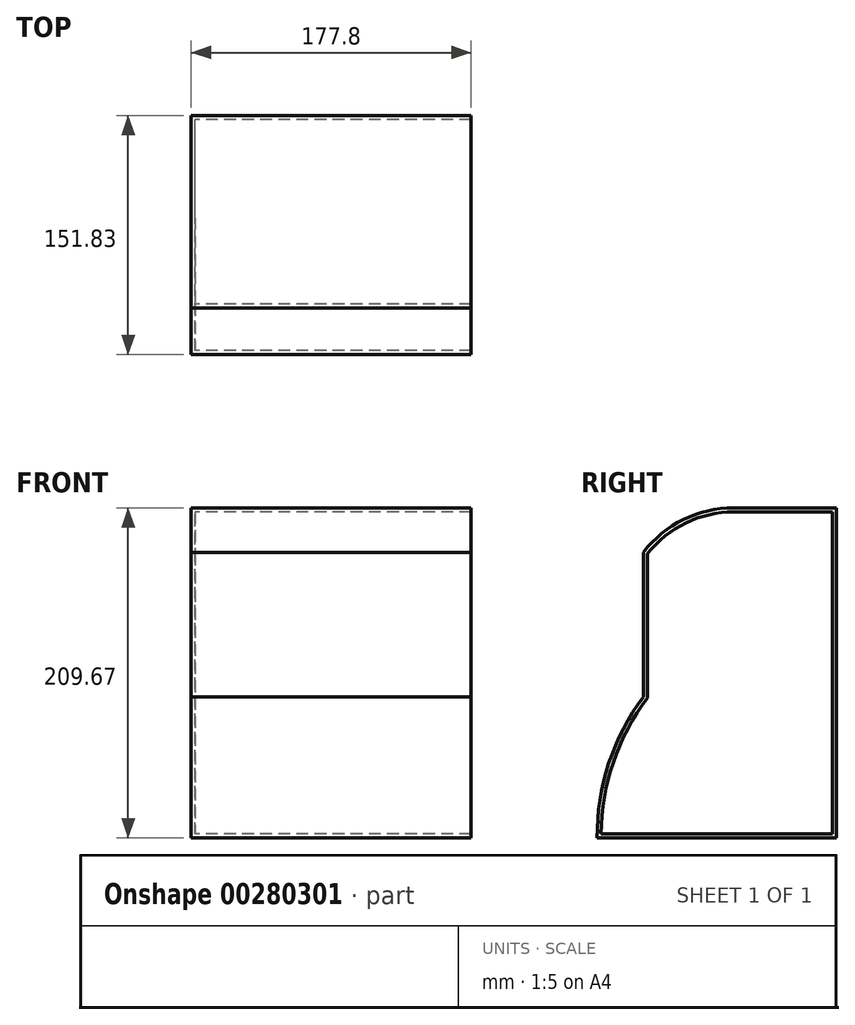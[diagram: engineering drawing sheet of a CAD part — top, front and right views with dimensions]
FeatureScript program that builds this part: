
annotation { "Feature Type Name" : "Feature", "Feature Type Description" : "" }
export const myFeature = defineFeature(function(context is Context, id is Id, definition is map)
    precondition{}
    {
        {
            var Q0;
            Q0=qCreatedBy(makeId("Right.planeOp"),FACE);
            var sketch = newSketch(context, id + "F0", { "sketchPlane" : qUnion([Q0])});
            skArc(sketch, "E0", {"start": v(33.16, 61.72) * mm, "mid": v(1.2, 54.3) * mm, "end": v(-24.2, 33.55) * mm});
            skLineSegment(sketch, "E1", {"start": v(-24.2, 33.55) * mm, "end": v(-24.2, -58.2) * mm});
            skArc(sketch, "E2", {"start": v(-24.2, -58.2) * mm, "mid": v(-46.26, -100.66) * mm, "end": v(-53.58, -147.95) * mm});
            skLineSegment(sketch, "E3", {"start": v(33.16, 61.72) * mm, "end": v(98.24, 61.72) * mm});
            skLineSegment(sketch, "E4", {"start": v(-53.58, -147.95) * mm, "end": v(98.24, -147.95) * mm});
            skLineSegment(sketch, "E5", {"start": v(98.24, -147.95) * mm, "end": v(98.24, 61.72) * mm});
            skSolve(sketch);
        }
        {
            var Q0;
            Q0 = qSketchRegion(id + "F0", true);
            extrude(context, id + "F1", {"entities" : qUnion([Q0]), "depth" : 177.8 * mm});
        }
        {
            var Q0;
            Q0=makeQuery(id+"F1.opExtrude","CAP_FACE",FACE,{"disambiguationData":[OSD([sQuery(id+"F0.wireOp",EDGE,"E0"),sQuery(id+"F0.wireOp",EDGE,"E1"),sQuery(id+"F0.wireOp",EDGE,"E2"),sQuery(id+"F0.wireOp",EDGE,"E3"),sQuery(id+"F0.wireOp",EDGE,"E4"),sQuery(id+"F0.wireOp",EDGE,"E5")])],"isStart":false});
            shell(context, id + "F2", {"entities" : qUnion([Q0]), "thickness" : 2.54 * mm});
        }
    });
